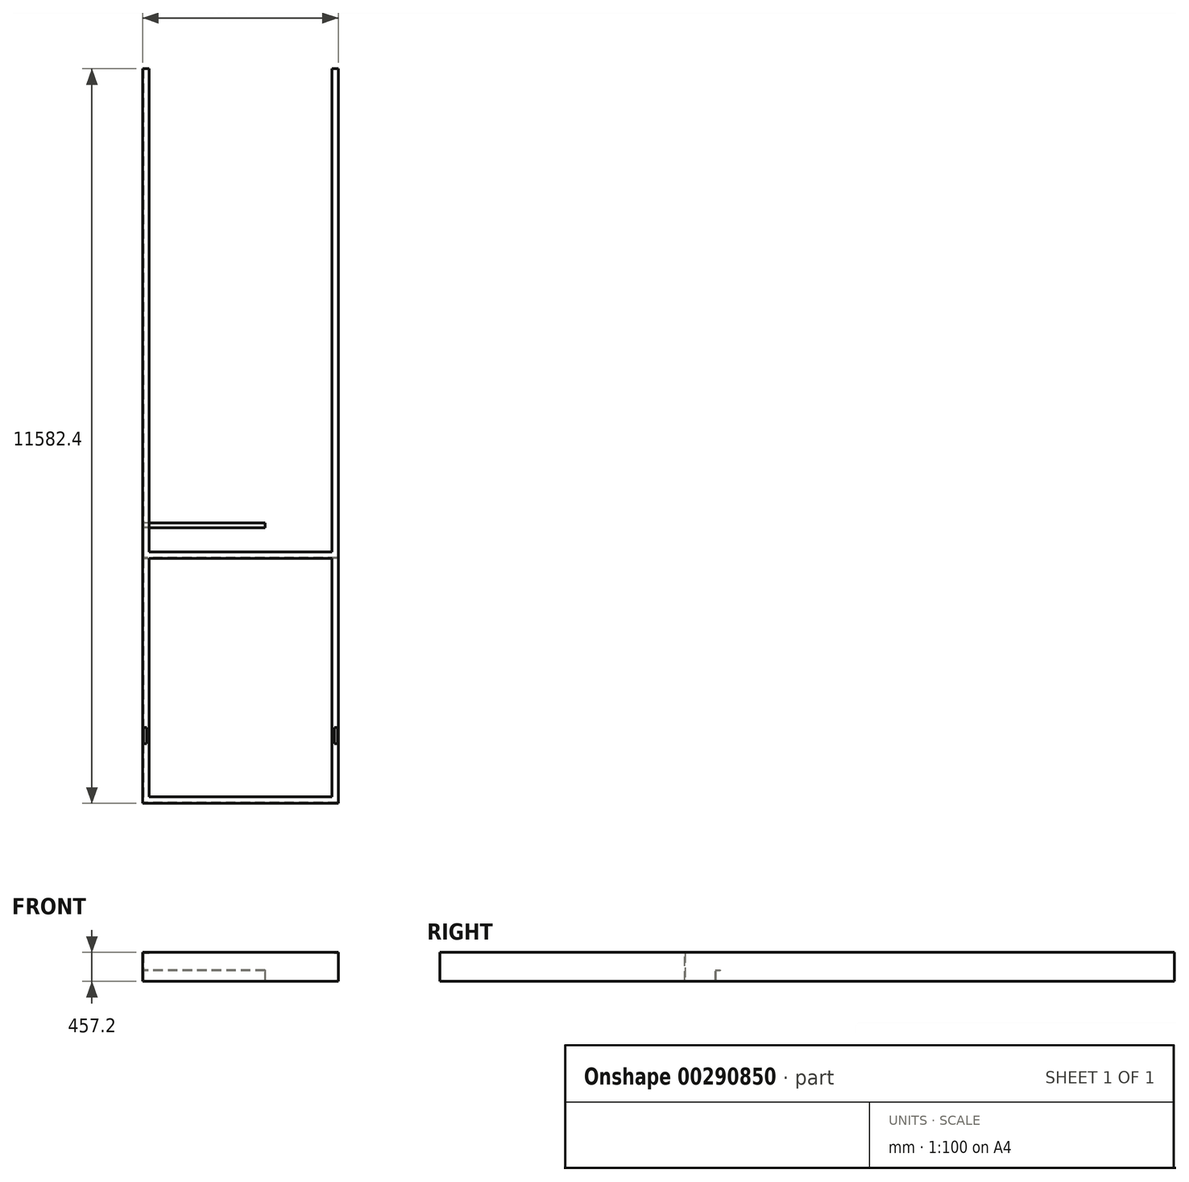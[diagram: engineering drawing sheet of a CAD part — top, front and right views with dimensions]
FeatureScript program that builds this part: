
annotation { "Feature Type Name" : "Feature", "Feature Type Description" : "" }
export const myFeature = defineFeature(function(context is Context, id is Id, definition is map)
    precondition{}
    {
        {
            var Q0;
            Q0=qCreatedBy(makeId("Top.planeOp"),FACE);
            var sketch = newSketch(context, id + "F0", { "sketchPlane" : qUnion([Q0])});
            skLineSegment(sketch, "E0.bottom", {"start": v(0, 0) * mm, "end": v(3086.1, 0) * mm});
            skLineSegment(sketch, "E0.top", {"start": v(0, 11582.4) * mm, "end": v(3086.1, 11582.4) * mm});
            skLineSegment(sketch, "E0.left", {"start": v(0, 0) * mm, "end": v(0, 11582.4) * mm});
            skLineSegment(sketch, "E0.right", {"start": v(3086.1, 0) * mm, "end": v(3086.1, 11582.4) * mm});
            skLineSegment(sketch, "E1", {"start": v(0, 3860.8) * mm, "end": v(3086.1, 3860.8) * mm});
            skLineSegment(sketch, "E2", {"start": v(0, 7721.6) * mm, "end": v(3086.1, 7721.6) * mm});
            skLineSegment(sketch, "E3", {"start": v(1543.05, 11582.4) * mm, "end": v(1543.05, 0) * mm, "construction": true});
            skLineSegment(sketch, "E4", {"start": v(0, 4343.4) * mm, "end": v(1930.4, 4343.4) * mm});
            skSolve(sketch);
        }
        {
            var Q0;
            Q0=qCreatedBy(makeId("Front.planeOp"),FACE);
            var sketch = newSketch(context, id + "F1", { "sketchPlane" : qUnion([Q0])});
            skLineSegment(sketch, "E5", {"start": v(0, 0) * mm, "end": v(0, 457.2) * mm});
            skLineSegment(sketch, "E6", {"start": v(0, 457.2) * mm, "end": v(101.6, 457.2) * mm});
            skLineSegment(sketch, "E7", {"start": v(101.6, 457.2) * mm, "end": v(101.6, 445.77) * mm});
            skLineSegment(sketch, "E8", {"start": v(101.6, 445.77) * mm, "end": v(11.43, 445.77) * mm});
            skLineSegment(sketch, "E9", {"start": v(11.43, 445.77) * mm, "end": v(11.43, 11.43) * mm});
            skLineSegment(sketch, "E10", {"start": v(11.43, 11.43) * mm, "end": v(101.6, 11.43) * mm});
            skLineSegment(sketch, "E11", {"start": v(101.6, 11.43) * mm, "end": v(101.6, 0) * mm});
            skLineSegment(sketch, "E12", {"start": v(101.6, 0) * mm, "end": v(0, 0) * mm});
            skSolve(sketch);
        }
        {
            var Q0;
            Q0 = qSketchRegion(id + "F1", true);
            var Q1;
            Q1=sQuery(id+"F0.wireOp",VERTEX,"E0.left.end");
            extrude(context, id + "F2", {"entities" : qUnion([Q0]), "endBound" : BoundingType.UP_TO_VERTEX, "oppositeDirection" : true, "endBoundEntityVertex" : qUnion([Q1]), "depth" : 25.4 * mm});
        }
        {
            var Q0;
            Q0=sQuery(id+"F0.wireOp",EDGE,"E3");
            cPoint(context, id + "F3", {"entities" : qUnion([Q0]), "parameter" : 0.5});
        }
        {
            var Q0;
            Q0=qCreatedBy(makeId("Right.planeOp"),FACE);
            var Q1;
            Q1 = qCreatedBy(id + "F3" ,VERTEX);
            cPlane(context, id + "F4", {"entities" : qUnion([Q0, Q1]), "cplaneType" : CPlaneType.PLANE_POINT, "offset" : 25.4 * mm, "width" : 152.4 * mm, "height" : 152.4 * mm});
        }
        {
            var Q0;
            Q0=qCreatedBy(makeId("Right.planeOp"),FACE);
            var sketch = newSketch(context, id + "F5", { "sketchPlane" : qUnion([Q0])});
            skLineSegment(sketch, "E13", {"start": v(0, 0) * mm, "end": v(0, 457.2) * mm});
            skLineSegment(sketch, "E14", {"start": v(0, 457.2) * mm, "end": v(101.6, 457.2) * mm});
            skLineSegment(sketch, "E15", {"start": v(101.6, 457.2) * mm, "end": v(101.6, 445.77) * mm});
            skLineSegment(sketch, "E16", {"start": v(101.6, 445.77) * mm, "end": v(11.43, 445.77) * mm});
            skLineSegment(sketch, "E17", {"start": v(11.43, 445.77) * mm, "end": v(11.43, 11.43) * mm});
            skLineSegment(sketch, "E18", {"start": v(11.43, 11.43) * mm, "end": v(101.6, 11.43) * mm});
            skLineSegment(sketch, "E19", {"start": v(101.6, 11.43) * mm, "end": v(101.6, 0) * mm});
            skLineSegment(sketch, "E20", {"start": v(101.6, 0) * mm, "end": v(0, 0) * mm});
            skLineSegment(sketch, "E21", {"start": v(3860.8, 0) * mm, "end": v(3860.8, 457.2) * mm});
            skLineSegment(sketch, "E22", {"start": v(3860.8, 457.2) * mm, "end": v(3962.4, 457.2) * mm});
            skLineSegment(sketch, "E23", {"start": v(3962.4, 457.2) * mm, "end": v(3962.4, 445.77) * mm});
            skLineSegment(sketch, "E24", {"start": v(3962.4, 445.77) * mm, "end": v(3872.23, 445.77) * mm});
            skLineSegment(sketch, "E25", {"start": v(3872.23, 445.77) * mm, "end": v(3872.23, 11.43) * mm});
            skLineSegment(sketch, "E26", {"start": v(3872.23, 11.43) * mm, "end": v(3962.4, 11.43) * mm});
            skLineSegment(sketch, "E27", {"start": v(3962.4, 11.43) * mm, "end": v(3962.4, 0) * mm});
            skLineSegment(sketch, "E28", {"start": v(3962.4, 0) * mm, "end": v(3860.8, 0) * mm});
            skSolve(sketch);
        }
        {
            var Q0;
            Q0 = qSketchRegion(id + "F5", true);
            var Q1;
            Q1=sQuery(id+"F0.wireOp",VERTEX,"E0.right.start");
            extrude(context, id + "F6", {"entities" : qUnion([Q0]), "operationType" : NewBodyOperationType.ADD, "endBound" : BoundingType.UP_TO_VERTEX, "endBoundEntityVertex" : qUnion([Q1]), "depth" : 25.4 * mm});
        }
        {
            var Q0;
            Q0=makeQuery(id+"F2.opExtrude","SWEPT_BODY",BODY,{"disambiguationData":[OSD([sQuery(id+"F1.wireOp",EDGE,"E5"),sQuery(id+"F1.wireOp",EDGE,"E6"),sQuery(id+"F1.wireOp",EDGE,"E7"),sQuery(id+"F1.wireOp",EDGE,"E8"),sQuery(id+"F1.wireOp",EDGE,"E9"),sQuery(id+"F1.wireOp",EDGE,"E10"),sQuery(id+"F1.wireOp",EDGE,"E11"),sQuery(id+"F1.wireOp",EDGE,"E12")])]});
            var Q1;
            Q1=qCreatedBy(id+"F4.planeOp",FACE);
            mirror(context, id + "F7", {"operationType" : NewBodyOperationType.ADD, "entities" : qUnion([Q0]), "mirrorPlane" : qUnion([Q1])});
        }
        {
            var Q0;
            Q0=sQuery(id+"F0.wireOp",EDGE,"E3");
            cPoint(context, id + "F8", {"entities" : qUnion([Q0]), "parameter" : 0.5});
        }
        {
            var Q0;
            Q0=qCreatedBy(makeId("Front.planeOp"),FACE);
            var Q1;
            Q1 = qCreatedBy(id + "F8" ,VERTEX);
            cPlane(context, id + "F9", {"entities" : qUnion([Q0, Q1]), "cplaneType" : CPlaneType.PLANE_POINT, "offset" : 25.4 * mm, "width" : 152.4 * mm, "height" : 152.4 * mm});
        }
        {
            var Q0;
            {var subQ0=sQuery(id+"F5.wireOp",EDGE,"E22");var subQ1=sQuery(id+"F5.wireOp",EDGE,"E14");var subQ2=makeQuery(id+"F6.boolean.opBoolean","MERGE",FACE,{"derivedFrom":[makeQuery(id+"F2.opExtrude","SWEPT_FACE",FACE,{"disambiguationData":[OSD([sQuery(id+"F1.wireOp",EDGE,"E6")])]}),makeQuery(id+"F6.opExtrude","SWEPT_FACE",FACE,{"disambiguationData":[OSD([subQ1])]}),makeQuery(id+"F6.opExtrude","SWEPT_FACE",FACE,{"disambiguationData":[OSD([subQ0])]})]});Q0=makeQuery(id+"F2iEFiSfP4QHRge_1.1.F6.boolean.opBoolean","MERGE",FACE,{"derivedFrom":[makeQuery(id+"F7.boolean.opBoolean","MERGE",FACE,{"derivedFrom":[subQ2,makeQuery(id+"F7.opPattern","COPY",FACE,{"derivedFrom":subQ2,"instanceName":"1"})]}),makeQuery(id+"F2iEFiSfP4QHRge_1.1.F6.opExtrude","SWEPT_FACE",FACE,{"disambiguationData":[OSD([subQ1])]}),makeQuery(id+"F2iEFiSfP4QHRge_1.1.F6.opExtrude","SWEPT_FACE",FACE,{"disambiguationData":[OSD([subQ0])]})]});}
            var sketch = newSketch(context, id + "F10", { "sketchPlane" : qUnion([Q0])});
            skLineSegment(sketch, "E29.bottom", {"start": v(11.43, 939.8) * mm, "end": v(62.23, 939.8) * mm});
            skLineSegment(sketch, "E29.top", {"start": v(11.43, 1193.8) * mm, "end": v(62.23, 1193.8) * mm});
            skLineSegment(sketch, "E29.left", {"start": v(11.43, 939.8) * mm, "end": v(11.43, 1193.8) * mm});
            skLineSegment(sketch, "E29.right", {"start": v(62.23, 939.8) * mm, "end": v(62.23, 1193.8) * mm});
            skLineSegment(sketch, "E30", {"start": v(62.23, 1193.8) * mm, "end": v(11.43, 939.8) * mm, "construction": true});
            skLineSegment(sketch, "E31", {"start": v(62.23, 939.8) * mm, "end": v(11.43, 1193.8) * mm, "construction": true});
            skPoint(sketch, "E32", {"position": v(36.83, 1066.8) * mm});
            skLineSegment(sketch, "E33.MirrorCS", {"start": v(3074.67, 939.8) * mm, "end": v(3023.87, 939.8) * mm});
            skLineSegment(sketch, "E34.MirrorCS", {"start": v(3074.67, 1193.8) * mm, "end": v(3023.87, 1193.8) * mm});
            skPoint(sketch, "E35.MirrorP", {"position": v(3049.27, 1066.8) * mm});
            skLineSegment(sketch, "E36.MirrorCS", {"start": v(3023.87, 939.8) * mm, "end": v(3074.67, 1193.8) * mm, "construction": true});
            skLineSegment(sketch, "E37.MirrorCS", {"start": v(3023.87, 1193.8) * mm, "end": v(3074.67, 939.8) * mm, "construction": true});
            skLineSegment(sketch, "E38.MirrorCS", {"start": v(3023.87, 939.8) * mm, "end": v(3023.87, 1193.8) * mm});
            skLineSegment(sketch, "E39.MirrorCS", {"start": v(3074.67, 939.8) * mm, "end": v(3074.67, 1193.8) * mm});
            skSolve(sketch);
        }
        {
            var Q0;
            Q0 = qSketchRegion(id + "F10", true);
            extrude(context, id + "F11", {"entities" : qUnion([Q0]), "operationType" : NewBodyOperationType.REMOVE, "endBound" : BoundingType.UP_TO_NEXT, "oppositeDirection" : true, "depth" : 25.4 * mm});
        }
        {
            var Q0;
            Q0=qCreatedBy(makeId("Right.planeOp"),FACE);
            var sketch = newSketch(context, id + "F12", { "sketchPlane" : qUnion([Q0])});
            skLineSegment(sketch, "E40", {"start": v(4343.4, 0) * mm, "end": v(4343.4, 177.8) * mm});
            skLineSegment(sketch, "E41", {"start": v(4343.4, 177.8) * mm, "end": v(4419.6, 177.8) * mm});
            skLineSegment(sketch, "E42", {"start": v(4419.6, 177.8) * mm, "end": v(4419.6, 168.27) * mm});
            skLineSegment(sketch, "E43", {"start": v(4419.6, 168.28) * mm, "end": v(4352.93, 168.28) * mm});
            skLineSegment(sketch, "E44", {"start": v(4352.93, 168.27) * mm, "end": v(4352.93, 9.53) * mm});
            skLineSegment(sketch, "E45", {"start": v(4352.93, 9.53) * mm, "end": v(4419.6, 9.53) * mm});
            skLineSegment(sketch, "E46", {"start": v(4419.6, 9.53) * mm, "end": v(4419.6, 0) * mm});
            skLineSegment(sketch, "E47", {"start": v(4419.6, 0) * mm, "end": v(4343.4, 0) * mm});
            skSolve(sketch);
        }
        {
            var Q0;
            Q0 = qSketchRegion(id + "F12", true);
            extrude(context, id + "F13", {"entities" : qUnion([Q0]), "operationType" : NewBodyOperationType.ADD, "depth" : 1930.4 * mm});
        }
    });
